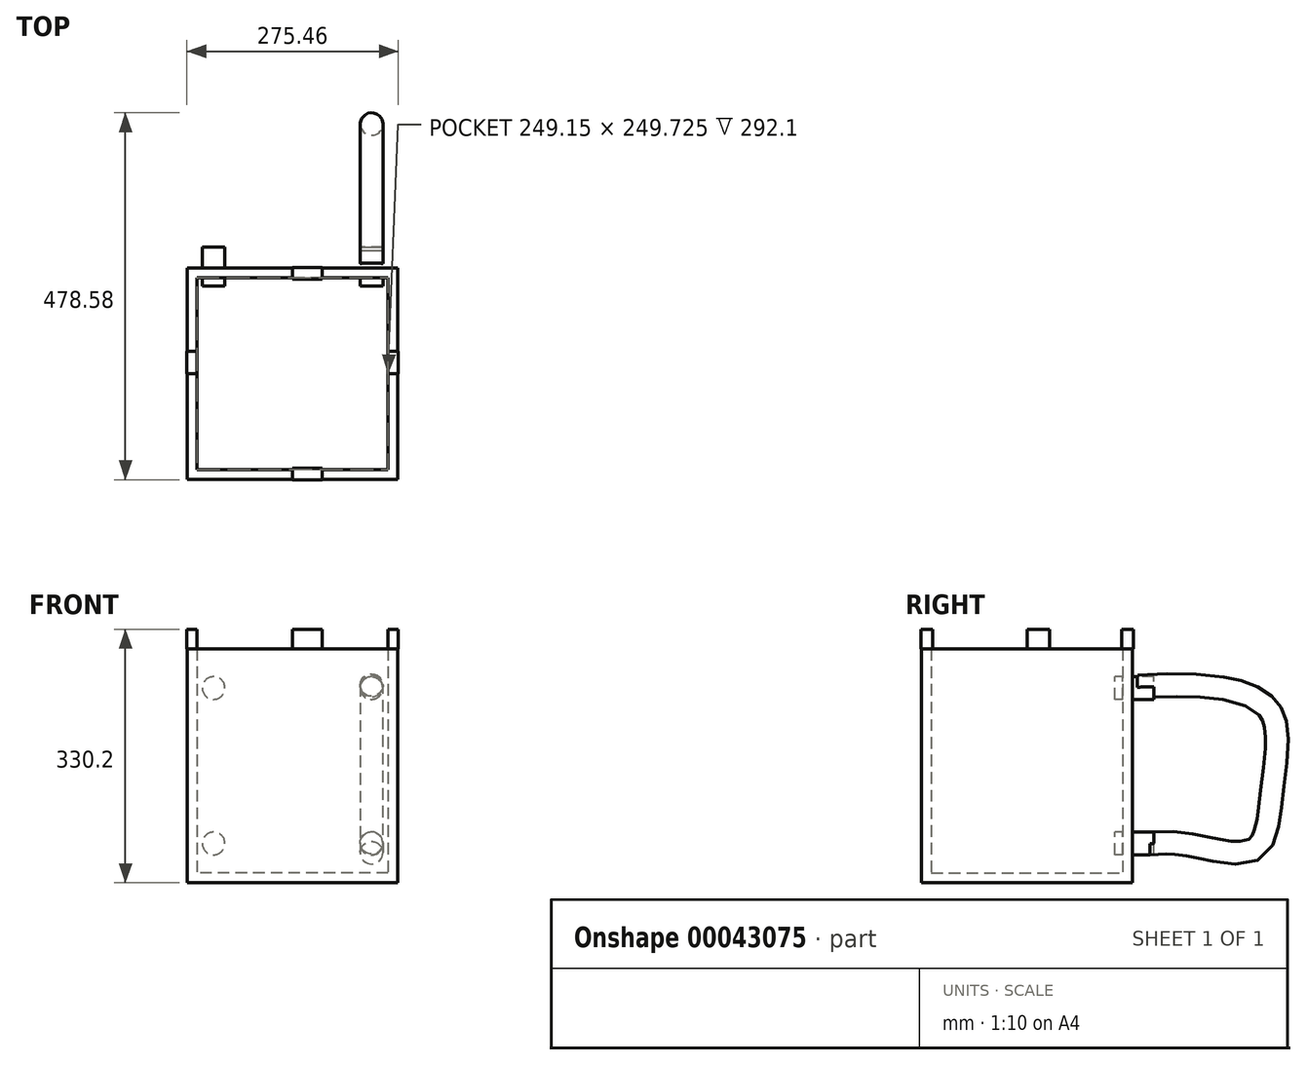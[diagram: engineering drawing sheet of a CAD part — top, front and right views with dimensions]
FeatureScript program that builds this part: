
annotation { "Feature Type Name" : "Feature", "Feature Type Description" : "" }
export const myFeature = defineFeature(function(context is Context, id is Id, definition is map)
    precondition{}
    {
        {
            var Q0;
            Q0=qCreatedBy(makeId("Front.planeOp"),FACE);
            cPlane(context, id + "F0", {"entities" : qUnion([Q0]), "cplaneType" : CPlaneType.OFFSET, "offset" : 139.7 * mm, "oppositeDirection" : true, "width" : 152.4 * mm, "height" : 152.4 * mm});
        }
        {
            var Q0;
            Q0=qCreatedBy(makeId("Top.planeOp"),FACE);
            var sketch = newSketch(context, id + "F1", { "sketchPlane" : qUnion([Q0])});
            skLineSegment(sketch, "E0.rect.bottom", {"start": v(137.27, -137.56) * mm, "end": v(-137.27, -137.56) * mm});
            skLineSegment(sketch, "E0.rect.top", {"start": v(137.27, 137.56) * mm, "end": v(-137.27, 137.56) * mm});
            skLineSegment(sketch, "E0.rect.left", {"start": v(137.27, -137.56) * mm, "end": v(137.27, 137.56) * mm});
            skLineSegment(sketch, "E0.rect.right", {"start": v(-137.27, -137.56) * mm, "end": v(-137.27, 137.56) * mm});
            skPoint(sketch, "E0.rect.middle", {"position": v(0, 0) * mm});
            skSolve(sketch);
        }
        {
            var Q0;
            Q0=makeQuery(id+"F1.imprint","IMPRINT",FACE,{"disambiguationData":[TD([[makeQuery(id+"F1.imprint","IMPRINT",EDGE,{"derivedFrom":sQuery(id+"F1.wireOp",EDGE,"E0.rect.bottom")}),-1.0]])]});
            extrude(context, id + "F2", {"entities" : qUnion([Q0]), "depth" : 152.4 * mm, "hasSecondDirection" : true, "secondDirectionOppositeDirection" : true, "secondDirectionDepth" : 152.4 * mm});
        }
        {
            var Q0;
            Q0=makeQuery(id+"F2.opExtrude","CAP_FACE",FACE,{"disambiguationData":[OSD([sQuery(id+"F1.wireOp",EDGE,"E0.rect.bottom"),sQuery(id+"F1.wireOp",EDGE,"E0.rect.top"),sQuery(id+"F1.wireOp",EDGE,"E0.rect.left"),sQuery(id+"F1.wireOp",EDGE,"E0.rect.right")])],"isStart":false});
            shell(context, id + "F3", {"entities" : qUnion([Q0]), "thickness" : 12.7 * mm});
        }
        {
            var Q0;
            Q0=qCreatedBy(id+"F0.planeOp",FACE);
            var sketch = newSketch(context, id + "F4", { "sketchPlane" : qUnion([Q0])});
            skLineSegment(sketch, "E1.rect.bottom", {"start": v(-102.88, -114.14) * mm, "end": v(102.88, -114.14) * mm});
            skLineSegment(sketch, "E1.rect.top", {"start": v(-102.88, 114.14) * mm, "end": v(102.88, 114.14) * mm});
            skLineSegment(sketch, "E1.rect.left", {"start": v(-102.88, -114.14) * mm, "end": v(-102.88, 114.14) * mm});
            skLineSegment(sketch, "E1.rect.right", {"start": v(102.88, -114.14) * mm, "end": v(102.88, 114.14) * mm});
            skPoint(sketch, "E1.rect.middle", {"position": v(0, 0) * mm});
            skLineSegment(sketch, "E2.rect.bottom", {"start": v(88.13, -101.33) * mm, "end": v(117.63, -101.33) * mm});
            skLineSegment(sketch, "E2.rect.top", {"start": v(88.13, 101.33) * mm, "end": v(117.63, 101.33) * mm});
            skLineSegment(sketch, "E2.rect.left", {"start": v(88.13, -101.33) * mm, "end": v(88.13, 101.33) * mm});
            skLineSegment(sketch, "E2.rect.right", {"start": v(117.63, -101.33) * mm, "end": v(117.63, 101.33) * mm});
            skPoint(sketch, "E2.rect.middle", {"position": v(102.88, 0) * mm});
            skLineSegment(sketch, "E3", {"start": v(0, 114.14) * mm, "end": v(0, -114.14) * mm});
            skLineSegment(sketch, "E4.MirrorCS", {"start": v(-117.63, -101.33) * mm, "end": v(-117.63, 101.33) * mm});
            skLineSegment(sketch, "E5.MirrorCS", {"start": v(-88.13, -101.33) * mm, "end": v(-88.13, 101.33) * mm});
            skLineSegment(sketch, "E6.MirrorCS", {"start": v(-88.13, 101.33) * mm, "end": v(-117.63, 101.33) * mm});
            skLineSegment(sketch, "E7.MirrorCS", {"start": v(-88.13, -101.33) * mm, "end": v(-117.63, -101.33) * mm});
            skCircle(sketch, "E8", {"center": v(102.88, 101.33) * mm, "radius": 14.75 * mm});
            skLineSegment(sketch, "E9", {"start": v(102.88, 0) * mm, "end": v(88.13, 0) * mm});
            skLineSegment(sketch, "E10", {"start": v(88.13, 0) * mm, "end": v(117.63, 0) * mm});
            skPoint(sketch, "E11.MirrorP", {"position": v(-102.88, 0) * mm});
            skLineSegment(sketch, "E12.MirrorCS", {"start": v(-88.13, 0) * mm, "end": v(-117.63, 0) * mm});
            skCircle(sketch, "E13.MirrorC", {"center": v(-102.88, 101.33) * mm, "radius": 14.75 * mm});
            skCircle(sketch, "E14.MirrorC", {"center": v(-102.88, -101.33) * mm, "radius": 14.75 * mm});
            skCircle(sketch, "E15.MirrorC", {"center": v(102.88, -101.33) * mm, "radius": 14.75 * mm});
            skSolve(sketch);
        }
        {
            var Q0;
            {var subQ1=sQuery(id+"F4.wireOp",EDGE,"E1.rect.right");var subQ3=sQuery(id+"F4.wireOp",EDGE,"E2.rect.bottom");var subQ5=makeQuery(id+"F4.imprint","INTERSECT",VERTEX,{"derivedFrom":[subQ1,subQ3]});Q0=makeQuery(id+"F4.imprint","IMPRINT",FACE,{"disambiguationData":[TD([[makeQuery(id+"F4.imprint","IMPRINT",EDGE,{"disambiguationData":[TD([[subQ5,-1.0]])],"derivedFrom":subQ1}),1.0]])]});}
            var Q1;
            {var subQ1=sQuery(id+"F4.wireOp",EDGE,"E1.rect.bottom");var subQ5=sQuery(id+"F4.wireOp",EDGE,"E1.rect.right");var subQ7=makeQuery(id+"F4.imprint","INTERSECT",VERTEX,{"derivedFrom":[subQ1,subQ5]});Q1=makeQuery(id+"F4.imprint","IMPRINT",FACE,{"disambiguationData":[TD([[makeQuery(id+"F4.imprint","IMPRINT",EDGE,{"disambiguationData":[TD([[subQ7,1.0]])],"derivedFrom":subQ1}),1.0]])]});}
            var Q2;
            {var subQ1=sQuery(id+"F4.wireOp",EDGE,"E1.rect.left");var subQ3=sQuery(id+"F4.wireOp",EDGE,"E7.MirrorCS");var subQ5=makeQuery(id+"F4.imprint","INTERSECT",VERTEX,{"derivedFrom":[subQ3,subQ1]});Q2=makeQuery(id+"F4.imprint","IMPRINT",FACE,{"disambiguationData":[TD([[makeQuery(id+"F4.imprint","IMPRINT",EDGE,{"disambiguationData":[TD([[subQ5,-1.0]])],"derivedFrom":subQ1}),1.0]])]});}
            var Q3;
            {var subQ1=sQuery(id+"F4.wireOp",EDGE,"E1.rect.top");var subQ5=sQuery(id+"F4.wireOp",EDGE,"E1.rect.right");var subQ7=makeQuery(id+"F4.imprint","INTERSECT",VERTEX,{"derivedFrom":[subQ1,subQ5]});Q3=makeQuery(id+"F4.imprint","IMPRINT",FACE,{"disambiguationData":[TD([[makeQuery(id+"F4.imprint","IMPRINT",EDGE,{"disambiguationData":[TD([[subQ7,1.0]])],"derivedFrom":subQ1}),1.0]])]});}
            var Q4;
            {var subQ1=sQuery(id+"F4.wireOp",EDGE,"E1.rect.top");var subQ5=sQuery(id+"F4.wireOp",EDGE,"E1.rect.left");var subQ7=makeQuery(id+"F4.imprint","INTERSECT",VERTEX,{"derivedFrom":[subQ1,subQ5]});Q4=makeQuery(id+"F4.imprint","IMPRINT",FACE,{"disambiguationData":[TD([[makeQuery(id+"F4.imprint","IMPRINT",EDGE,{"disambiguationData":[TD([[subQ7,-1.0]])],"derivedFrom":subQ1}),1.0]])]});}
            var Q5;
            {var subQ1=sQuery(id+"F4.wireOp",EDGE,"E1.rect.right");var subQ3=sQuery(id+"F4.wireOp",EDGE,"E2.rect.bottom");var subQ5=makeQuery(id+"F4.imprint","INTERSECT",VERTEX,{"derivedFrom":[subQ1,subQ3]});Q5=makeQuery(id+"F4.imprint","IMPRINT",FACE,{"disambiguationData":[TD([[makeQuery(id+"F4.imprint","IMPRINT",EDGE,{"disambiguationData":[TD([[subQ5,-1.0]])],"derivedFrom":subQ1}),-1.0]])]});}
            var Q6;
            {var subQ1=sQuery(id+"F4.wireOp",EDGE,"E1.rect.right");var subQ3=sQuery(id+"F4.wireOp",EDGE,"E8");var subQ5=makeQuery(id+"F4.imprint","INTERSECT",VERTEX,{"derivedFrom":[subQ1,subQ3]});Q6=makeQuery(id+"F4.imprint","IMPRINT",FACE,{"disambiguationData":[TD([[makeQuery(id+"F4.imprint","IMPRINT",EDGE,{"disambiguationData":[TD([[subQ5,-1.0]])],"derivedFrom":subQ1}),1.0]])]});}
            var Q7;
            {var subQ1=sQuery(id+"F4.wireOp",EDGE,"E1.rect.top");var subQ5=sQuery(id+"F4.wireOp",EDGE,"E1.rect.right");var subQ7=makeQuery(id+"F4.imprint","INTERSECT",VERTEX,{"derivedFrom":[subQ1,subQ5]});Q7=makeQuery(id+"F4.imprint","IMPRINT",FACE,{"disambiguationData":[TD([[makeQuery(id+"F4.imprint","IMPRINT",EDGE,{"disambiguationData":[TD([[subQ7,1.0]])],"derivedFrom":subQ1}),-1.0]])]});}
            var Q8;
            {var subQ0=sQuery(id+"F4.wireOp",EDGE,"E8");var subQ1=sQuery(id+"F4.wireOp",EDGE,"E1.rect.right");var subQ2=makeQuery(id+"F4.imprint","INTERSECT",VERTEX,{"derivedFrom":[subQ1,subQ0]});Q8=makeQuery(id+"F4.imprint","IMPRINT",FACE,{"disambiguationData":[TD([[makeQuery(id+"F4.imprint","IMPRINT",EDGE,{"disambiguationData":[TD([[subQ2,-1.0]])],"derivedFrom":subQ1}),-1.0]])]});}
            var Q9;
            {var subQ1=sQuery(id+"F4.wireOp",EDGE,"E1.rect.left");var subQ3=sQuery(id+"F4.wireOp",EDGE,"E7.MirrorCS");var subQ5=makeQuery(id+"F4.imprint","INTERSECT",VERTEX,{"derivedFrom":[subQ3,subQ1]});Q9=makeQuery(id+"F4.imprint","IMPRINT",FACE,{"disambiguationData":[TD([[makeQuery(id+"F4.imprint","IMPRINT",EDGE,{"disambiguationData":[TD([[subQ5,-1.0]])],"derivedFrom":subQ1}),-1.0]])]});}
            var Q10;
            {var subQ0=sQuery(id+"F4.wireOp",EDGE,"E13.MirrorC");var subQ1=sQuery(id+"F4.wireOp",EDGE,"E1.rect.left");var subQ2=makeQuery(id+"F4.imprint","INTERSECT",VERTEX,{"derivedFrom":[subQ1,subQ0]});Q10=makeQuery(id+"F4.imprint","IMPRINT",FACE,{"disambiguationData":[TD([[makeQuery(id+"F4.imprint","IMPRINT",EDGE,{"disambiguationData":[TD([[subQ2,-1.0]])],"derivedFrom":subQ1}),1.0]])]});}
            var Q11;
            {var subQ0=sQuery(id+"F4.wireOp",EDGE,"E13.MirrorC");var subQ1=sQuery(id+"F4.wireOp",EDGE,"E1.rect.left");var subQ2=makeQuery(id+"F4.imprint","INTERSECT",VERTEX,{"derivedFrom":[subQ1,subQ0]});Q11=makeQuery(id+"F4.imprint","IMPRINT",FACE,{"disambiguationData":[TD([[makeQuery(id+"F4.imprint","IMPRINT",EDGE,{"disambiguationData":[TD([[subQ2,-1.0]])],"derivedFrom":subQ1}),-1.0]])]});}
            var Q12;
            {var subQ1=sQuery(id+"F4.wireOp",EDGE,"E1.rect.bottom");var subQ5=sQuery(id+"F4.wireOp",EDGE,"E1.rect.left");var subQ7=makeQuery(id+"F4.imprint","INTERSECT",VERTEX,{"derivedFrom":[subQ1,subQ5]});Q12=makeQuery(id+"F4.imprint","IMPRINT",FACE,{"disambiguationData":[TD([[makeQuery(id+"F4.imprint","IMPRINT",EDGE,{"disambiguationData":[TD([[subQ7,-1.0]])],"derivedFrom":subQ1}),-1.0]])]});}
            var Q13;
            {var subQ0=sQuery(id+"F4.wireOp",EDGE,"E1.rect.left");var subQ3=sQuery(id+"F4.wireOp",EDGE,"E1.rect.bottom");var subQ4=makeQuery(id+"F4.imprint","INTERSECT",VERTEX,{"derivedFrom":[subQ3,subQ0]});Q13=makeQuery(id+"F4.imprint","IMPRINT",FACE,{"disambiguationData":[TD([[makeQuery(id+"F4.imprint","IMPRINT",EDGE,{"disambiguationData":[TD([[subQ4,-1.0]])],"derivedFrom":subQ3}),1.0]])]});}
            var Q14;
            {var subQ1=sQuery(id+"F4.wireOp",EDGE,"E1.rect.bottom");var subQ5=sQuery(id+"F4.wireOp",EDGE,"E1.rect.right");var subQ7=makeQuery(id+"F4.imprint","INTERSECT",VERTEX,{"derivedFrom":[subQ1,subQ5]});Q14=makeQuery(id+"F4.imprint","IMPRINT",FACE,{"disambiguationData":[TD([[makeQuery(id+"F4.imprint","IMPRINT",EDGE,{"disambiguationData":[TD([[subQ7,1.0]])],"derivedFrom":subQ1}),-1.0]])]});}
            var Q15;
            {var subQ1=sQuery(id+"F4.wireOp",EDGE,"E1.rect.top");var subQ5=sQuery(id+"F4.wireOp",EDGE,"E1.rect.left");var subQ7=makeQuery(id+"F4.imprint","INTERSECT",VERTEX,{"derivedFrom":[subQ1,subQ5]});Q15=makeQuery(id+"F4.imprint","IMPRINT",FACE,{"disambiguationData":[TD([[makeQuery(id+"F4.imprint","IMPRINT",EDGE,{"disambiguationData":[TD([[subQ7,-1.0]])],"derivedFrom":subQ1}),-1.0]])]});}
            extrude(context, id + "F5", {"entities" : qUnion([Q0, Q1, Q2, Q3, Q4, Q5, Q6, Q7, Q8, Q9, Q10, Q11, Q12, Q13, Q14, Q15]), "operationType" : NewBodyOperationType.ADD, "oppositeDirection" : true, "depth" : 25.4 * mm, "hasSecondDirection" : true, "secondDirectionOppositeDirection" : false, "secondDirectionDepth" : 25.4 * mm});
        }
        {
            var Q0;
            Q0=qCreatedBy(makeId("Right.planeOp"),FACE);
            cPlane(context, id + "F6", {"entities" : qUnion([Q0]), "cplaneType" : CPlaneType.OFFSET, "offset" : 101.6 * mm, "width" : 152.4 * mm, "height" : 152.4 * mm});
        }
        {
            var Q0;
            Q0=qCreatedBy(id+"F6.planeOp",FACE);
            var sketch = newSketch(context, id + "F7", { "sketchPlane" : qUnion([Q0])});
            skFitSpline(sketch, "E16", {"points": [v(160.33, -102.23) * mm, v(209.93, -103.35) * mm, v(295.77, -109.48) * mm, v(319.73, -31.45) * mm, v(318.06, 70) * mm, v(246.16, 102.88) * mm, v(143.6, 104) * mm], "startDerivative": vector(333.22, 27.14) * mm, "endDerivative": vector(-552.88, -25.6) * mm});
            skSolve(sketch);
        }
        {
            var Q0;
            Q0=makeQuery(id+"F5.opExtrude","CAP_FACE",FACE,{"disambiguationData":[OSD([sQuery(id+"F4.wireOp",EDGE,"E15.MirrorC")])],"isStart":false});
            var Q1;
            Q1=sQuery(id+"F7.wireOp",EDGE,"E16");
            sweep(context, id + "F8", {"operationType" : NewBodyOperationType.ADD, "profiles" : qUnion([Q0]), "path" : qUnion([Q1])});
        }
        {
            var Q0;
            Q0=makeQuery(id+"F2.opExtrude","CAP_FACE",FACE,{"disambiguationData":[OSD([sQuery(id+"F1.wireOp",EDGE,"E0.rect.bottom"),sQuery(id+"F1.wireOp",EDGE,"E0.rect.top"),sQuery(id+"F1.wireOp",EDGE,"E0.rect.left"),sQuery(id+"F1.wireOp",EDGE,"E0.rect.right")])],"isStart":false});
            cPlane(context, id + "F9", {"entities" : qUnion([Q0]), "cplaneType" : CPlaneType.OFFSET, "offset" : 0 * mm, "width" : 152.4 * mm, "height" : 152.4 * mm});
        }
        {
            var Q0;
            Q0=qCreatedBy(id+"F9.planeOp",FACE);
            var sketch = newSketch(context, id + "F10", { "sketchPlane" : qUnion([Q0])});
            skLineSegment(sketch, "E17.bottom", {"start": v(0, 123.06) * mm, "end": v(38.55, 123.06) * mm});
            skLineSegment(sketch, "E17.top", {"start": v(0, 138.38) * mm, "end": v(38.55, 138.38) * mm});
            skLineSegment(sketch, "E17.left", {"start": v(0, 123.06) * mm, "end": v(0, 138.38) * mm});
            skLineSegment(sketch, "E17.right", {"start": v(38.55, 123.06) * mm, "end": v(38.55, 138.38) * mm});
            skLineSegment(sketch, "E18", {"start": v(0, 0) * mm, "end": v(73.14, 0) * mm});
            skLineSegment(sketch, "E19.MirrorCS", {"start": v(0, -123.06) * mm, "end": v(38.55, -123.06) * mm});
            skLineSegment(sketch, "E20.MirrorCS", {"start": v(0, -138.38) * mm, "end": v(38.55, -138.38) * mm});
            skLineSegment(sketch, "E21.MirrorCS", {"start": v(38.55, -123.06) * mm, "end": v(38.55, -138.38) * mm});
            skLineSegment(sketch, "E22.MirrorCS", {"start": v(0, -123.06) * mm, "end": v(0, -138.38) * mm});
            skLineSegment(sketch, "E23", {"start": v(0, 0) * mm, "end": v(0, 73.99) * mm});
            skLineSegment(sketch, "E24.bottom", {"start": v(-124.62, 0) * mm, "end": v(-137.73, 0) * mm});
            skLineSegment(sketch, "E24.top", {"start": v(-124.62, 29.42) * mm, "end": v(-137.73, 29.42) * mm});
            skLineSegment(sketch, "E24.left", {"start": v(-124.62, 0) * mm, "end": v(-124.62, 29.42) * mm});
            skLineSegment(sketch, "E24.right", {"start": v(-137.73, 0) * mm, "end": v(-137.73, 29.42) * mm});
            skLineSegment(sketch, "E25.MirrorCS", {"start": v(124.62, 0) * mm, "end": v(124.62, 29.42) * mm});
            skLineSegment(sketch, "E26.MirrorCS", {"start": v(137.73, 0) * mm, "end": v(137.73, 29.42) * mm});
            skLineSegment(sketch, "E27.MirrorCS", {"start": v(124.62, 29.42) * mm, "end": v(137.73, 29.42) * mm});
            skLineSegment(sketch, "E28.MirrorCS", {"start": v(124.62, 0) * mm, "end": v(137.73, 0) * mm});
            skSolve(sketch);
        }
        {
            var Q0;
            Q0=makeQuery(id+"F10.imprint","IMPRINT",FACE,{"disambiguationData":[TD([[makeQuery(id+"F10.imprint","IMPRINT",EDGE,{"derivedFrom":sQuery(id+"F10.wireOp",EDGE,"E24.bottom")}),-1.0]])]});
            var Q1;
            Q1=makeQuery(id+"F10.imprint","IMPRINT",FACE,{"disambiguationData":[TD([[makeQuery(id+"F10.imprint","IMPRINT",EDGE,{"derivedFrom":sQuery(id+"F10.wireOp",EDGE,"E25.MirrorCS")}),-1.0]])]});
            var Q2;
            Q2=makeQuery(id+"F10.imprint","IMPRINT",FACE,{"disambiguationData":[TD([[makeQuery(id+"F10.imprint","IMPRINT",EDGE,{"derivedFrom":sQuery(id+"F10.wireOp",EDGE,"E19.MirrorCS")}),-1.0]])]});
            var Q3;
            Q3=makeQuery(id+"F10.imprint","IMPRINT",FACE,{"disambiguationData":[TD([[makeQuery(id+"F10.imprint","IMPRINT",EDGE,{"derivedFrom":sQuery(id+"F10.wireOp",EDGE,"E17.bottom")}),1.0]])]});
            extrude(context, id + "F11", {"entities" : qUnion([Q0, Q1, Q2, Q3]), "depth" : 25.4 * mm});
        }
    });
